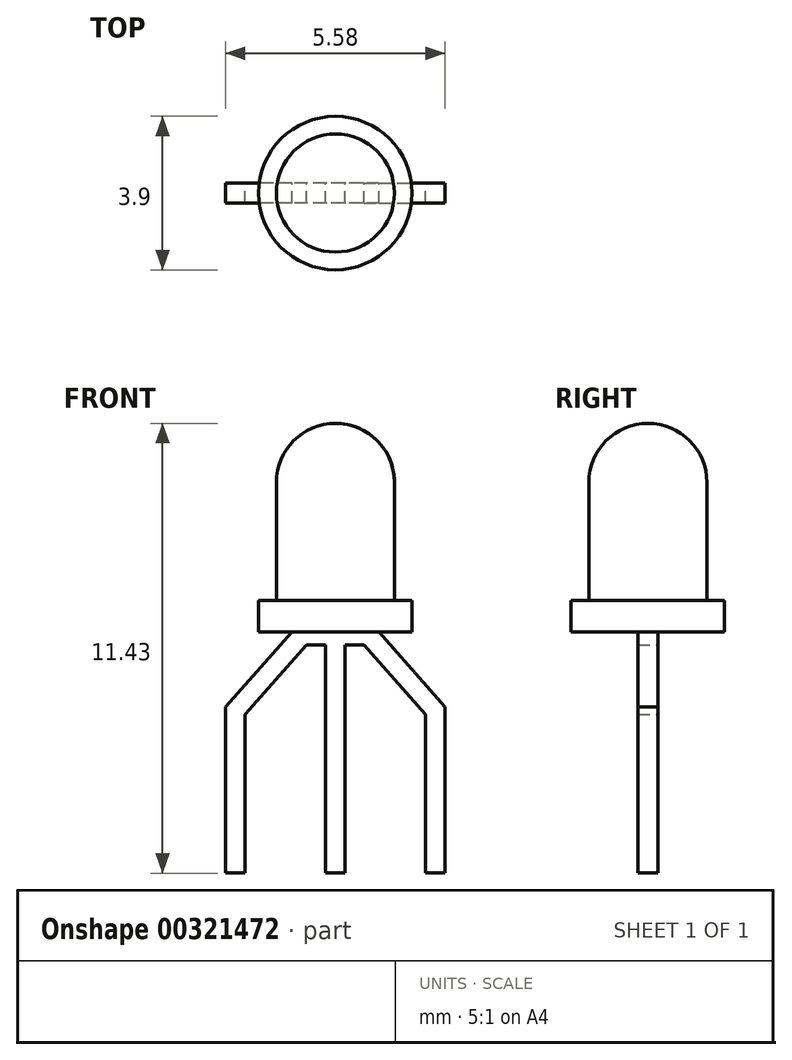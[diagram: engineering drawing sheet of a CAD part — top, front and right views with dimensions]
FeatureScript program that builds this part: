
annotation { "Feature Type Name" : "Feature", "Feature Type Description" : "" }
export const myFeature = defineFeature(function(context is Context, id is Id, definition is map)
    precondition{}
    {
        {
            var Q0;
            Q0=qCreatedBy(makeId("Top.planeOp"),FACE);
            var sketch = newSketch(context, id + "F0", { "sketchPlane" : qUnion([Q0])});
            skCircle(sketch, "E0", {"center": v(0, 0) * mm, "radius": 1.95 * mm});
            skSolve(sketch);
        }
        {
            var Q0;
            Q0 = qSketchRegion(id + "F0", true);
            extrude(context, id + "F1", {"entities" : qUnion([Q0]), "depth" : .8 * mm});
        }
        {
            var Q0;
            Q0=makeQuery(id+"F1.opExtrude","CAP_FACE",FACE,{"disambiguationData":[OSD([sQuery(id+"F0.wireOp",EDGE,"E0")])],"isStart":false});
            var sketch = newSketch(context, id + "F2", { "sketchPlane" : qUnion([Q0])});
            skCircle(sketch, "E1", {"center": v(0, 0) * mm, "radius": 1.5 * mm});
            skSolve(sketch);
        }
        {
            var Q0;
            Q0 = qSketchRegion(id + "F2", true);
            extrude(context, id + "F3", {"entities" : qUnion([Q0]), "operationType" : NewBodyOperationType.ADD, "depth" : 4.5 * mm});
        }
        {
            var Q0;
            Q0=makeQuery(id+"F3.opExtrude","CAP_EDGE",EDGE,{"disambiguationData":[OSD([sQuery(id+"F2.wireOp",EDGE,"E1")])],"isStart":false});
            fillet(context, id + "F4", {"entities" : qUnion([Q0]), "radius" : 1.5 * mm, "tangentPropagation" : true, "allowEdgeOverflow" : false});
        }
        {
            var Q0;
            Q0=qCreatedBy(makeId("Front.planeOp"),FACE);
            var sketch = newSketch(context, id + "F5", { "sketchPlane" : qUnion([Q0])});
            skLineSegment(sketch, "E2", {"start": v(0, -0.9) * mm, "end": v(0, -7.84) * mm});
            skLineSegment(sketch, "E3", {"start": v(-2.54, -0.9) * mm, "end": v(-2.54, -7.96) * mm});
            skLineSegment(sketch, "E4", {"start": v(2.54, -0.97) * mm, "end": v(2.54, -7.53) * mm});
            skLineSegment(sketch, "E5.0", {"start": v(2.29, -0.97) * mm, "end": v(2.3, -6.13) * mm});
            skLineSegment(sketch, "E6.0", {"start": v(2.8, -0.97) * mm, "end": v(2.8, -6.13) * mm});
            skLineSegment(sketch, "E7.0", {"start": v(-0.25, -0.33) * mm, "end": v(-0.25, -7.84) * mm});
            skLineSegment(sketch, "E8.0", {"start": v(0.25, -0.33) * mm, "end": v(0.25, -7.84) * mm});
            skLineSegment(sketch, "E9.0", {"start": v(-2.3, -0.9) * mm, "end": v(-2.3, -7.96) * mm});
            skLineSegment(sketch, "E10.0", {"start": v(-2.8, -0.9) * mm, "end": v(-2.79, -7.96) * mm});
            skLineSegment(sketch, "E11", {"start": v(1.1, 0) * mm, "end": v(2.8, -1.9) * mm});
            skLineSegment(sketch, "E12.MirrorCS", {"start": v(-1.1, 0) * mm, "end": v(-2.8, -1.9) * mm});
            skLineSegment(sketch, "E13.0", {"start": v(0.73, -0.33) * mm, "end": v(2.42, -2.24) * mm});
            skLineSegment(sketch, "E14.0", {"start": v(-0.73, -0.33) * mm, "end": v(-2.42, -2.24) * mm});
            skLineSegment(sketch, "E15", {"start": v(0.73, -0.33) * mm, "end": v(-0.73, -0.33) * mm});
            skLineSegment(sketch, "E16", {"start": v(1.1, 0) * mm, "end": v(-1.1, 0) * mm});
            skLineSegment(sketch, "E17", {"start": v(2.8, -6.13) * mm, "end": v(2.3, -6.13) * mm});
            skLineSegment(sketch, "E18.trimOffspring", {"start": v(-2.3, -6.13) * mm, "end": v(-2.8, -6.13) * mm});
            skLineSegment(sketch, "E19.trimOffspring", {"start": v(0.25, -6.13) * mm, "end": v(-0.25, -6.13) * mm});
            skSolve(sketch);
        }
        {
            var Q0;
            Q0 = qSketchRegion(id + "F5", true);
            extrude(context, id + "F6", {"entities" : qUnion([Q0]), "depth" : .25 * mm, "hasSecondDirection" : true, "secondDirectionOppositeDirection" : true, "secondDirectionDepth" : .25 * mm});
        }
    });
